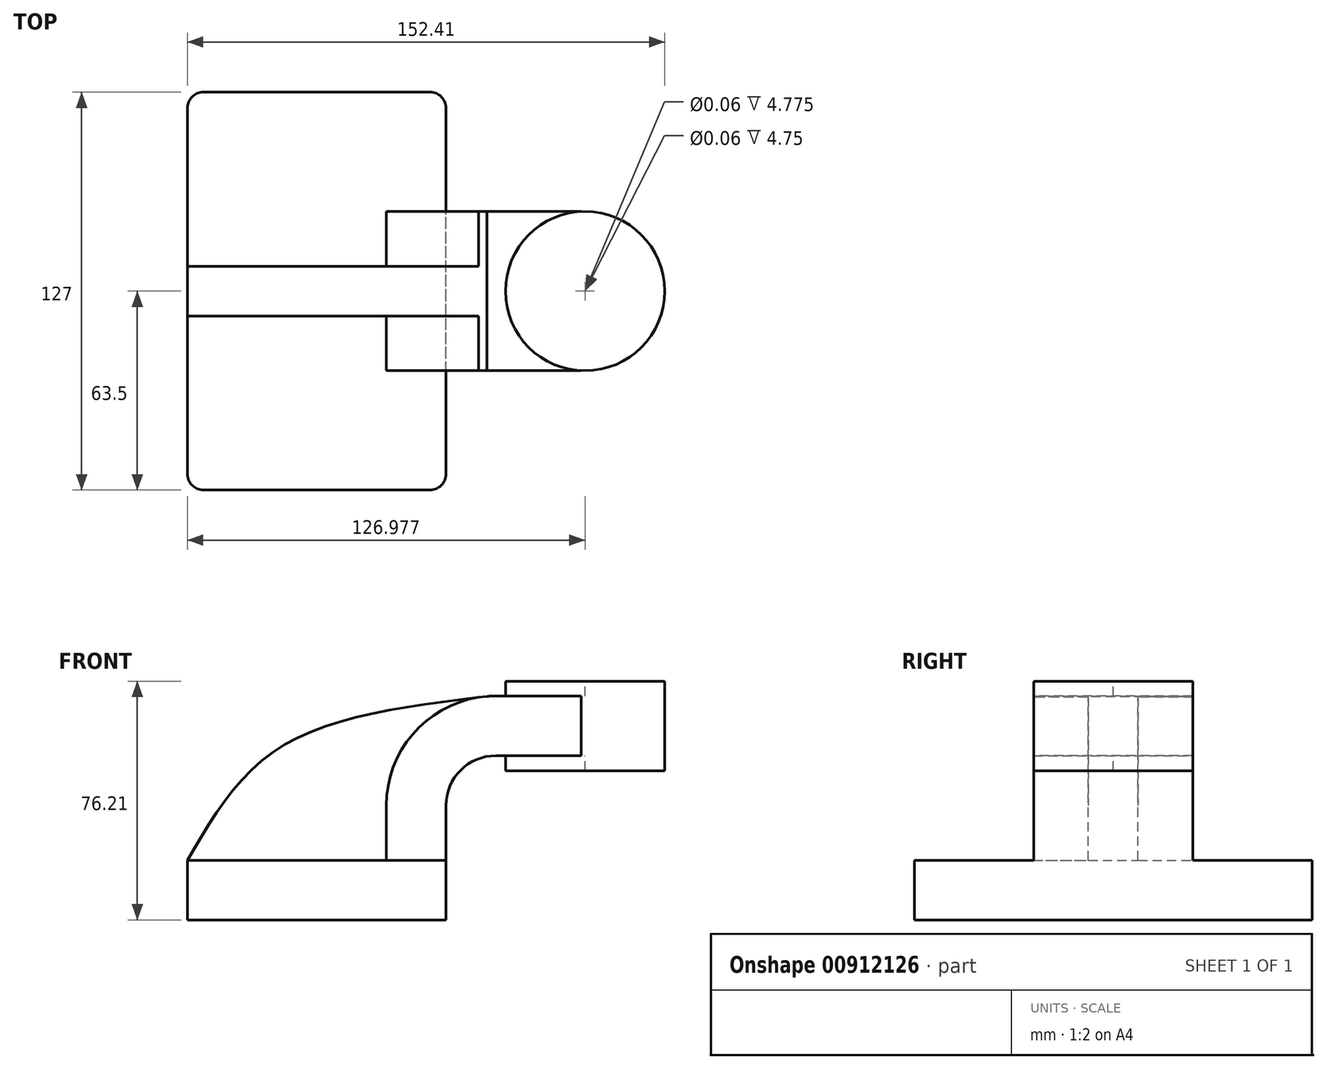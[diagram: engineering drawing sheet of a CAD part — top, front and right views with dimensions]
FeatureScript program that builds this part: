
annotation { "Feature Type Name" : "Feature", "Feature Type Description" : "" }
export const myFeature = defineFeature(function(context is Context, id is Id, definition is map)
    precondition{}
    {
        {
            var Q0;
            Q0=qCreatedBy(makeId("Front.planeOp"),FACE);
            var sketch = newSketch(context, id + "F0", { "sketchPlane" : qUnion([Q0])});
            skLineSegment(sketch, "E0.bottom", {"start": v(41.27, 9.53) * mm, "end": v(-41.28, 9.53) * mm});
            skLineSegment(sketch, "E0.top", {"start": v(41.28, -9.52) * mm, "end": v(-41.27, -9.52) * mm});
            skLineSegment(sketch, "E0.left", {"start": v(41.28, 9.53) * mm, "end": v(41.28, -9.52) * mm});
            skLineSegment(sketch, "E0.right", {"start": v(-41.28, 9.53) * mm, "end": v(-41.27, -9.52) * mm});
            skPoint(sketch, "E0.middle", {"position": v(0, 0) * mm});
            skLineSegment(sketch, "E1.bottom", {"start": v(60.33, 38.1) * mm, "end": v(111.13, 38.1) * mm});
            skLineSegment(sketch, "E1.top", {"start": v(60.33, 66.68) * mm, "end": v(111.13, 66.68) * mm});
            skLineSegment(sketch, "E1.left", {"start": v(60.33, 38.1) * mm, "end": v(60.33, 66.68) * mm});
            skLineSegment(sketch, "E1.right", {"start": v(111.13, 38.1) * mm, "end": v(111.12, 66.68) * mm});
            skPoint(sketch, "E1.middle", {"position": v(85.73, 52.39) * mm});
            skLineSegment(sketch, "E2", {"start": v(41.27, 9.53) * mm, "end": v(41.27, 27) * mm});
            skArc(sketch, "E3", {"start": v(41.27, 27) * mm, "mid": v(45.92, 38.23) * mm, "end": v(57.15, 42.88) * mm});
            skLineSegment(sketch, "E4", {"start": v(57.15, 42.88) * mm, "end": v(85.72, 42.88) * mm});
            skLineSegment(sketch, "E5.0", {"start": v(57.15, 61.93) * mm, "end": v(85.72, 61.93) * mm});
            skArc(sketch, "E5.1", {"start": v(22.23, 27) * mm, "mid": v(32.45, 51.7) * mm, "end": v(57.15, 61.93) * mm});
            skLineSegment(sketch, "E5.2", {"start": v(22.23, 9.53) * mm, "end": v(22.23, 27) * mm});
            skFitSpline(sketch, "E6", {"points": [v(-41.28, 9.52) * mm, v(-11.74, 45.49) * mm, v(54.37, 61.81) * mm], "startDerivative": vector(52.71, 90.7) * mm, "endDerivative": vector(135.94, 16.26) * mm});
            skLineSegment(sketch, "E7", {"start": v(85.72, 42.88) * mm, "end": v(85.72, 61.93) * mm});
            skLineSegment(sketch, "E8", {"start": v(85.72, 61.93) * mm, "end": v(85.72, 66.68) * mm});
            skLineSegment(sketch, "E9", {"start": v(85.72, 42.88) * mm, "end": v(85.73, 38.1) * mm});
            skSolve(sketch);
        }
        {
            var Q0;
            Q0=makeQuery(id+"F0.imprint","IMPRINT",FACE,{"disambiguationData":[TD([[makeQuery(id+"F0.imprint","IMPRINT",EDGE,{"derivedFrom":sQuery(id+"F0.wireOp",EDGE,"E0.top")}),-1.0]])]});
            extrude(context, id + "F1", {"entities" : qUnion([Q0]), "endBound" : BoundingType.SYMMETRIC, "depth" : 127 * mm, "offsetDistance" : 25.4 * mm});
        }
        {
            var Q0;
            {var subQ1=sQuery(id+"F0.wireOp",EDGE,"E2");Q0=makeQuery(id+"F0.imprint","IMPRINT",FACE,{"disambiguationData":[TD([[makeQuery(id+"F0.imprint","IMPRINT",EDGE,{"derivedFrom":subQ1}),1.0]])]});}
            var Q1;
            Q1 = qSketchRegion(id + "F3", true);
            extrude(context, id + "F2", {"entities" : qUnion([Q0, Q1]), "operationType" : NewBodyOperationType.ADD, "endBound" : BoundingType.SYMMETRIC, "depth" : 50.8 * mm, "offsetDistance" : 25.4 * mm});
        }
        {
            var Q0;
            Q0=qCreatedBy(makeId("Front.planeOp"),FACE);
            var sketch = newSketch(context, id + "F3", { "sketchPlane" : qUnion([Q0])});
            skLineSegment(sketch, "E10", {"start": v(85.7, 61.75) * mm, "end": v(85.7, 43.25) * mm});
            skSolve(sketch);
        }
        {
            var Q0;
            {var subQ5=sQuery(id+"F0.wireOp",EDGE,"E7");Q0=makeQuery(id+"F0.imprint","IMPRINT",FACE,{"disambiguationData":[TD([[makeQuery(id+"F0.imprint","IMPRINT",EDGE,{"derivedFrom":subQ5}),1.0]])]});}
            extrude(context, id + "F4", {"entities" : qUnion([Q0]), "operationType" : NewBodyOperationType.ADD, "endBound" : BoundingType.SYMMETRIC, "depth" : 50.8 * mm, "offsetDistance" : 25.4 * mm});
        }
        {
            var Q0;
            {var subQ3=sQuery(id+"F0.wireOp",EDGE,"E5.2");Q0=makeQuery(id+"F0.imprint","IMPRINT",FACE,{"disambiguationData":[TD([[makeQuery(id+"F0.imprint","IMPRINT",EDGE,{"derivedFrom":subQ3}),1.0]])]});}
            extrude(context, id + "F5", {"entities" : qUnion([Q0]), "operationType" : NewBodyOperationType.ADD, "endBound" : BoundingType.SYMMETRIC, "depth" : 15.88 * mm, "offsetDistance" : 25.4 * mm});
        }
        {
            var Q0;
            {var subQ0=sQuery(id+"F0.wireOp",EDGE,"E1.right");Q0=makeQuery(id+"F0.imprint","IMPRINT",FACE,{"disambiguationData":[TD([[makeQuery(id+"F0.imprint","IMPRINT",EDGE,{"derivedFrom":subQ0}),1.0]])]});}
            var Q1;
            Q1=sQuery(id+"F3.wireOp",EDGE,"E10");
            revolve(context, id + "F6", {"operationType" : NewBodyOperationType.ADD, "surfaceOperationType" : NewSurfaceOperationType.NEW, "entities" : qUnion([Q0]), "axis" : qUnion([Q1]), "revolveType" : RevolveType.FULL});
        }
        {
            var Q0;
            Q0=makeQuery(id+"F1.opExtrude","CAP_EDGE",EDGE,{"disambiguationData":[OSD([sQuery(id+"F0.wireOp",EDGE,"E0.left")])],"isStart":false});
            var Q1;
            Q1=makeQuery(id+"F1.opExtrude","CAP_EDGE",EDGE,{"disambiguationData":[OSD([sQuery(id+"F0.wireOp",EDGE,"E0.right")])],"isStart":false});
            var Q2;
            Q2=makeQuery(id+"F1.opExtrude","CAP_EDGE",EDGE,{"disambiguationData":[OSD([sQuery(id+"F0.wireOp",EDGE,"E0.left")])],"isStart":true});
            var Q3;
            Q3=makeQuery(id+"F1.opExtrude","CAP_EDGE",EDGE,{"disambiguationData":[OSD([sQuery(id+"F0.wireOp",EDGE,"E0.right")])],"isStart":true});
            fillet(context, id + "F7", {"entities" : qUnion([Q0, Q1, Q2, Q3]), "radius" : 5.08 * mm, "tangentPropagation" : true, "allowEdgeOverflow" : false});
        }
    });
